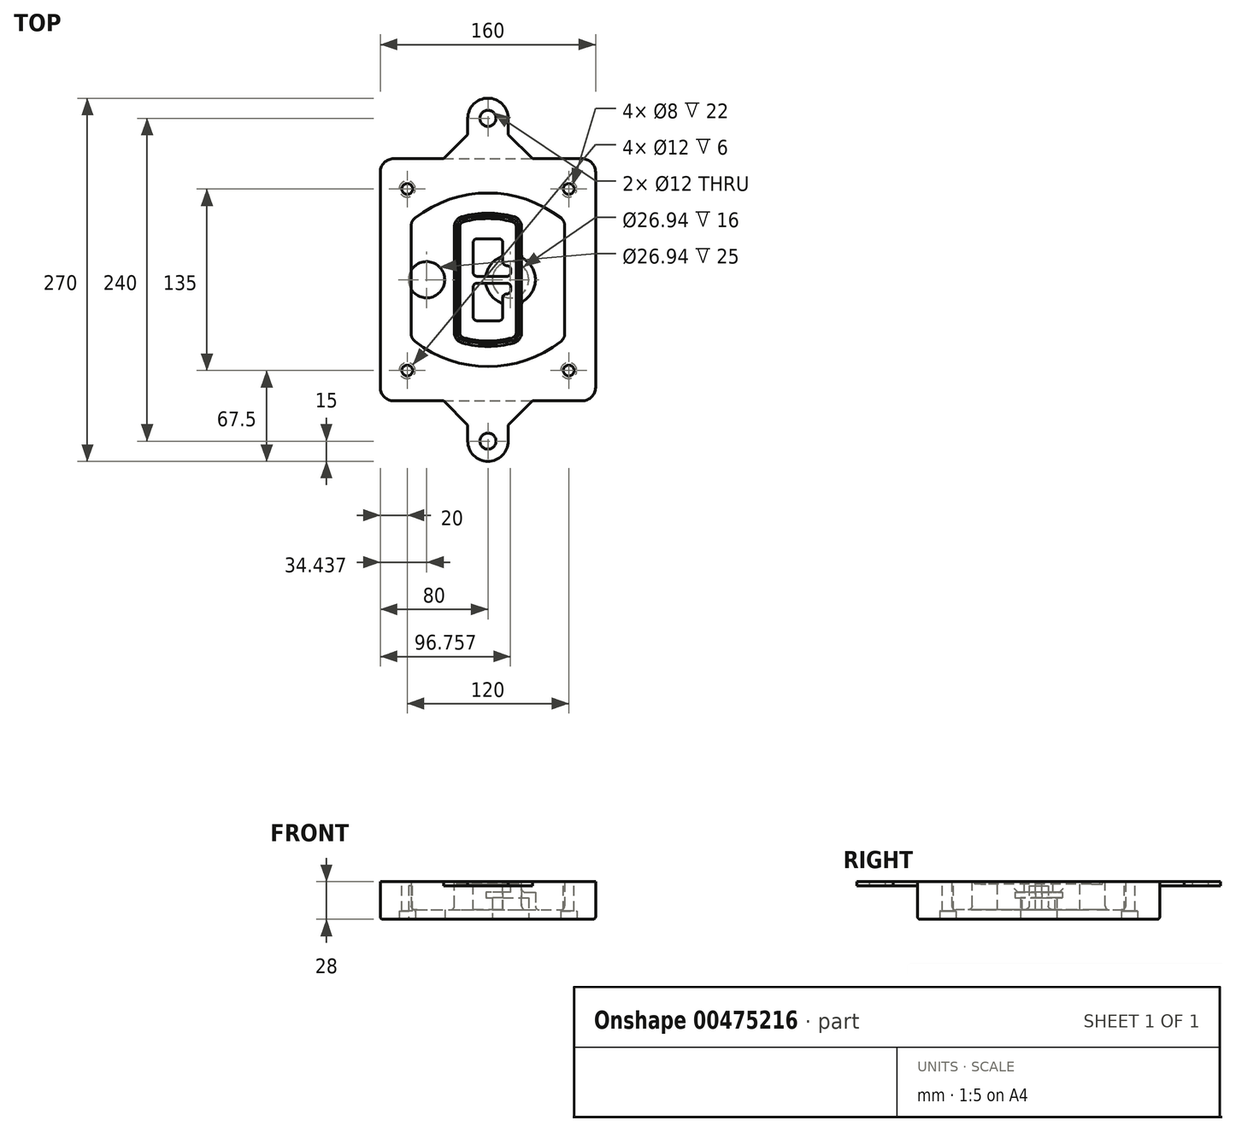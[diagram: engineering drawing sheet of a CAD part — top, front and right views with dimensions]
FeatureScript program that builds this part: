
annotation { "Feature Type Name" : "Feature", "Feature Type Description" : "" }
export const myFeature = defineFeature(function(context is Context, id is Id, definition is map)
    precondition{}
    {
        {
            var Q0;
            Q0=qCreatedBy(makeId("Top.planeOp"),FACE);
            var sketch = newSketch(context, id + "F0", { "sketchPlane" : qUnion([Q0])});
            skPoint(sketch, "E0.rect.middle", {"position": v(0, 0) * mm});
            skLineSegment(sketch, "E1.bottom", {"start": v(-70, -90) * mm, "end": v(70, -90) * mm});
            skLineSegment(sketch, "E1.top", {"start": v(-70, 90) * mm, "end": v(70, 90) * mm});
            skLineSegment(sketch, "E1.left", {"start": v(-80, -80) * mm, "end": v(-80, 80) * mm});
            skLineSegment(sketch, "E1.right", {"start": v(80, -80) * mm, "end": v(80, 80) * mm});
            skLineSegment(sketch, "E2", {"start": v(-80, 90) * mm, "end": v(80, -90) * mm, "construction": true});
            skLineSegment(sketch, "E3", {"start": v(80, 90) * mm, "end": v(-80, -90) * mm, "construction": true});
            skCircle(sketch, "E4", {"center": v(-60, 67.5) * mm, "radius": 4 * mm});
            skCircle(sketch, "E5", {"center": v(60, 67.5) * mm, "radius": 4 * mm});
            skCircle(sketch, "E6", {"center": v(60, -67.5) * mm, "radius": 4 * mm});
            skCircle(sketch, "E7", {"center": v(-60, -67.5) * mm, "radius": 4 * mm});
            skLineSegment(sketch, "E8", {"start": v(-60, 67.5) * mm, "end": v(60, 67.5) * mm, "construction": true});
            skLineSegment(sketch, "E9", {"start": v(60, 67.5) * mm, "end": v(60, -67.5) * mm, "construction": true});
            skLineSegment(sketch, "E10", {"start": v(60, -67.5) * mm, "end": v(-60, -67.5) * mm, "construction": true});
            skLineSegment(sketch, "E11", {"start": v(-60, -67.5) * mm, "end": v(-60, 67.5) * mm, "construction": true});
            skLineSegment(sketch, "E12", {"start": v(-60, 40.3) * mm, "end": v(-60, -40.3) * mm});
            skLineSegment(sketch, "E13", {"start": v(60, 40.3) * mm, "end": v(60, -40.3) * mm});
            skArc(sketch, "E14", {"start": v(56.15, 48.18) * mm, "mid": v(0, 67.5) * mm, "end": v(-56.15, 48.18) * mm});
            skArc(sketch, "E15", {"start": v(-56.15, -48.18) * mm, "mid": v(0, -67.5) * mm, "end": v(56.15, -48.18) * mm});
            skLineSegment(sketch, "E16", {"start": v(-60, 0) * mm, "end": v(60, 0) * mm, "construction": true});
            skPoint(sketch, "E17.visualSharp", {"position": v(-60, -45) * mm});
            skArc(sketch, "E17.filletArc", {"start": v(-60, -40.3) * mm, "mid": v(-58.99, -44.68) * mm, "end": v(-56.15, -48.18) * mm});
            skPoint(sketch, "E18.visualSharp", {"position": v(-60, 45) * mm});
            skArc(sketch, "E18.filletArc", {"start": v(-56.15, 48.18) * mm, "mid": v(-58.99, 44.68) * mm, "end": v(-60, 40.3) * mm});
            skPoint(sketch, "E19.visualSharp", {"position": v(60, 45) * mm});
            skArc(sketch, "E19.filletArc", {"start": v(60, 40.3) * mm, "mid": v(58.99, 44.68) * mm, "end": v(56.15, 48.18) * mm});
            skPoint(sketch, "E20.visualSharp", {"position": v(60, -45) * mm});
            skArc(sketch, "E20.filletArc", {"start": v(56.15, -48.18) * mm, "mid": v(58.99, -44.68) * mm, "end": v(60, -40.3) * mm});
            skPoint(sketch, "E21.visualSharp", {"position": v(-80, 90) * mm});
            skArc(sketch, "E21.filletArc", {"start": v(-70, 90) * mm, "mid": v(-77.07, 87.07) * mm, "end": v(-80, 80) * mm});
            skPoint(sketch, "E22.visualSharp", {"position": v(80, 90) * mm});
            skArc(sketch, "E22.filletArc", {"start": v(80, 80) * mm, "mid": v(77.07, 87.07) * mm, "end": v(70, 90) * mm});
            skPoint(sketch, "E23.visualSharp", {"position": v(80, -90) * mm});
            skArc(sketch, "E23.filletArc", {"start": v(70, -90) * mm, "mid": v(77.07, -87.07) * mm, "end": v(80, -80) * mm});
            skPoint(sketch, "E24.visualSharp", {"position": v(-80, -90) * mm});
            skArc(sketch, "E24.filletArc", {"start": v(-80, -80) * mm, "mid": v(-77.07, -87.07) * mm, "end": v(-70, -90) * mm});
            skArc(sketch, "E25.0", {"start": v(57, 40.3) * mm, "mid": v(56.3, 43.36) * mm, "end": v(54.3, 45.81) * mm});
            skLineSegment(sketch, "E25.1", {"start": v(57, 40.3) * mm, "end": v(57, -40.3) * mm});
            skArc(sketch, "E25.2", {"start": v(54.3, -45.81) * mm, "mid": v(56.3, -43.36) * mm, "end": v(57, -40.3) * mm});
            skArc(sketch, "E25.3", {"start": v(-54.3, -45.81) * mm, "mid": v(0, -64.5) * mm, "end": v(54.3, -45.81) * mm});
            skArc(sketch, "E25.4", {"start": v(-57, -40.3) * mm, "mid": v(-56.3, -43.36) * mm, "end": v(-54.3, -45.81) * mm});
            skArc(sketch, "E25.5", {"start": v(54.3, 45.81) * mm, "mid": v(0, 64.5) * mm, "end": v(-54.3, 45.81) * mm});
            skLineSegment(sketch, "E25.6", {"start": v(-57, 40.3) * mm, "end": v(-57, -40.3) * mm});
            skArc(sketch, "E25.7", {"start": v(-54.3, 45.81) * mm, "mid": v(-56.3, 43.36) * mm, "end": v(-57, 40.3) * mm});
            skArc(sketch, "E26.0", {"start": v(-58.62, 51.33) * mm, "mid": v(-62.58, 46.43) * mm, "end": v(-64, 40.3) * mm});
            skArc(sketch, "E26.1", {"start": v(58.62, 51.33) * mm, "mid": v(0, 71.5) * mm, "end": v(-58.62, 51.33) * mm});
            skArc(sketch, "E26.2", {"start": v(64, 40.3) * mm, "mid": v(62.58, 46.43) * mm, "end": v(58.62, 51.33) * mm});
            skLineSegment(sketch, "E26.3", {"start": v(64, 40.3) * mm, "end": v(64, -40.3) * mm});
            skArc(sketch, "E26.4", {"start": v(58.62, -51.33) * mm, "mid": v(62.58, -46.43) * mm, "end": v(64, -40.3) * mm});
            skLineSegment(sketch, "E26.5", {"start": v(-64, 40.3) * mm, "end": v(-64, -40.3) * mm});
            skArc(sketch, "E26.6", {"start": v(-58.62, -51.33) * mm, "mid": v(0, -71.5) * mm, "end": v(58.62, -51.33) * mm});
            skArc(sketch, "E26.7", {"start": v(-64, -40.3) * mm, "mid": v(-62.58, -46.43) * mm, "end": v(-58.62, -51.33) * mm});
            skSolve(sketch);
        }
        {
            var Q0;
            Q0=makeQuery(id+"F0.imprint","IMPRINT",FACE,{"disambiguationData":[TD([[makeQuery(id+"F0.imprint","IMPRINT",EDGE,{"derivedFrom":sQuery(id+"F0.wireOp",EDGE,"E1.bottom")}),1.0]])]});
            var Q1;
            Q1=makeQuery(id+"F0.imprint","IMPRINT",FACE,{"disambiguationData":[TD([[makeQuery(id+"F0.imprint","IMPRINT",EDGE,{"derivedFrom":sQuery(id+"F0.wireOp",EDGE,"E12")}),1.0]])]});
            var Q2;
            Q2=makeQuery(id+"F0.imprint","IMPRINT",FACE,{"disambiguationData":[TD([[makeQuery(id+"F0.imprint","IMPRINT",EDGE,{"derivedFrom":sQuery(id+"F0.wireOp",EDGE,"E25.0")}),1.0]])]});
            var Q3;
            Q3=makeQuery(id+"F0.imprint","IMPRINT",FACE,{"disambiguationData":[TD([[makeQuery(id+"F0.imprint","IMPRINT",EDGE,{"derivedFrom":sQuery(id+"F0.wireOp",EDGE,"E12")}),-1.0]])]});
            extrude(context, id + "F1", {"entities" : qUnion([Q0, Q1, Q2, Q3]), "oppositeDirection" : true, "depth" : 25 * mm});
        }
        {
            var Q0;
            Q0=makeQuery(id+"F0.imprint","IMPRINT",FACE,{"disambiguationData":[TD([[makeQuery(id+"F0.imprint","IMPRINT",EDGE,{"derivedFrom":sQuery(id+"F0.wireOp",EDGE,"E12")}),1.0]])]});
            extrude(context, id + "F2", {"entities" : qUnion([Q0]), "operationType" : NewBodyOperationType.ADD, "depth" : 3 * mm});
        }
        {
            var Q0;
            Q0=makeQuery(id+"F0.imprint","IMPRINT",FACE,{"disambiguationData":[TD([[makeQuery(id+"F0.imprint","IMPRINT",EDGE,{"derivedFrom":sQuery(id+"F0.wireOp",EDGE,"E25.0")}),1.0]])]});
            extrude(context, id + "F3", {"entities" : qUnion([Q0]), "operationType" : NewBodyOperationType.REMOVE, "oppositeDirection" : true, "depth" : 18 * mm});
        }
        {
            var Q0;
            Q0=makeQuery(id+"F2.opExtrude","CAP_FACE",FACE,{"disambiguationData":[OSD([sQuery(id+"F0.wireOp",EDGE,"E12"),sQuery(id+"F0.wireOp",EDGE,"E13"),sQuery(id+"F0.wireOp",EDGE,"E14"),sQuery(id+"F0.wireOp",EDGE,"E15"),sQuery(id+"F0.wireOp",EDGE,"E17.filletArc"),sQuery(id+"F0.wireOp",EDGE,"E18.filletArc"),sQuery(id+"F0.wireOp",EDGE,"E19.filletArc"),sQuery(id+"F0.wireOp",EDGE,"E20.filletArc"),sQuery(id+"F0.wireOp",EDGE,"E25.0"),sQuery(id+"F0.wireOp",EDGE,"E25.1"),sQuery(id+"F0.wireOp",EDGE,"E25.2"),sQuery(id+"F0.wireOp",EDGE,"E25.3"),sQuery(id+"F0.wireOp",EDGE,"E25.4"),sQuery(id+"F0.wireOp",EDGE,"E25.5"),sQuery(id+"F0.wireOp",EDGE,"E25.6"),sQuery(id+"F0.wireOp",EDGE,"E25.7")])],"isStart":false});
            var sketch = newSketch(context, id + "F4", { "sketchPlane" : qUnion([Q0])});
            skArc(sketch, "E27.0", {"start": v(-19.08, -46.97) * mm, "mid": v(0, -49.5) * mm, "end": v(19.08, -46.97) * mm});
            skArc(sketch, "E28.0", {"start": v(19.08, 46.97) * mm, "mid": v(0, 49.5) * mm, "end": v(-19.08, 46.97) * mm});
            skLineSegment(sketch, "E29", {"start": v(-25, 39.25) * mm, "end": v(-25, -39.25) * mm});
            skLineSegment(sketch, "E30", {"start": v(25, 39.25) * mm, "end": v(25, -39.25) * mm});
            skLineSegment(sketch, "E31", {"start": v(-25, 45.1) * mm, "end": v(25, 45.1) * mm, "construction": true});
            skLineSegment(sketch, "E32", {"start": v(-25, -45.1) * mm, "end": v(25, -45.1) * mm, "construction": true});
            skPoint(sketch, "E33.visualSharp", {"position": v(-25, 45.1) * mm});
            skArc(sketch, "E33.filletArc", {"start": v(-19.08, 46.97) * mm, "mid": v(-23.35, 44.11) * mm, "end": v(-25, 39.25) * mm});
            skPoint(sketch, "E34.visualSharp", {"position": v(25, 45.1) * mm});
            skArc(sketch, "E34.filletArc", {"start": v(25, 39.25) * mm, "mid": v(23.35, 44.11) * mm, "end": v(19.08, 46.97) * mm});
            skPoint(sketch, "E35.visualSharp", {"position": v(25, -45.1) * mm});
            skArc(sketch, "E35.filletArc", {"start": v(19.08, -46.97) * mm, "mid": v(23.35, -44.11) * mm, "end": v(25, -39.25) * mm});
            skPoint(sketch, "E36.visualSharp", {"position": v(-25, -45.1) * mm});
            skArc(sketch, "E36.filletArc", {"start": v(-25, -39.25) * mm, "mid": v(-23.35, -44.11) * mm, "end": v(-19.08, -46.97) * mm});
            skArc(sketch, "E37.0", {"start": v(54.3, 45.81) * mm, "mid": v(0, 64.5) * mm, "end": v(-54.3, 45.81) * mm});
            skArc(sketch, "E37.1", {"start": v(-54.3, 45.81) * mm, "mid": v(-56.3, 43.36) * mm, "end": v(-57, 40.3) * mm});
            skLineSegment(sketch, "E37.2", {"start": v(-57, 40.3) * mm, "end": v(-57, -40.3) * mm});
            skArc(sketch, "E37.3", {"start": v(-57, -40.3) * mm, "mid": v(-56.3, -43.36) * mm, "end": v(-54.3, -45.81) * mm});
            skArc(sketch, "E37.4", {"start": v(-54.3, -45.81) * mm, "mid": v(0, -64.5) * mm, "end": v(54.3, -45.81) * mm});
            skArc(sketch, "E37.5", {"start": v(54.3, -45.81) * mm, "mid": v(56.3, -43.36) * mm, "end": v(57, -40.3) * mm});
            skLineSegment(sketch, "E37.6", {"start": v(57, 40.3) * mm, "end": v(57, -40.3) * mm});
            skArc(sketch, "E37.7", {"start": v(57, 40.3) * mm, "mid": v(56.3, 43.36) * mm, "end": v(54.3, 45.81) * mm});
            skLineSegment(sketch, "E38.0", {"start": v(23, 39.25) * mm, "end": v(23, -39.25) * mm});
            skArc(sketch, "E38.1", {"start": v(18.56, -45.04) * mm, "mid": v(21.76, -42.9) * mm, "end": v(23, -39.25) * mm});
            skArc(sketch, "E38.2", {"start": v(-18.56, -45.04) * mm, "mid": v(0, -47.5) * mm, "end": v(18.56, -45.04) * mm});
            skArc(sketch, "E38.3", {"start": v(-23, -39.25) * mm, "mid": v(-21.76, -42.9) * mm, "end": v(-18.56, -45.04) * mm});
            skLineSegment(sketch, "E38.4", {"start": v(-23, 39.25) * mm, "end": v(-23, -39.25) * mm});
            skArc(sketch, "E38.5", {"start": v(23, 39.25) * mm, "mid": v(21.76, 42.9) * mm, "end": v(18.56, 45.04) * mm});
            skArc(sketch, "E38.6", {"start": v(-18.56, 45.04) * mm, "mid": v(-21.76, 42.9) * mm, "end": v(-23, 39.25) * mm});
            skArc(sketch, "E38.7", {"start": v(18.56, 45.04) * mm, "mid": v(0, 47.5) * mm, "end": v(-18.56, 45.04) * mm});
            skArc(sketch, "E39.0", {"start": v(21, 39.25) * mm, "mid": v(20.18, 41.68) * mm, "end": v(18.04, 43.1) * mm});
            skLineSegment(sketch, "E39.1", {"start": v(21, 39.25) * mm, "end": v(21, -39.25) * mm});
            skArc(sketch, "E39.2", {"start": v(18.04, -43.1) * mm, "mid": v(20.18, -41.68) * mm, "end": v(21, -39.25) * mm});
            skArc(sketch, "E39.3", {"start": v(-18.04, -43.1) * mm, "mid": v(0, -45.5) * mm, "end": v(18.04, -43.1) * mm});
            skArc(sketch, "E39.4", {"start": v(-21, -39.25) * mm, "mid": v(-20.18, -41.68) * mm, "end": v(-18.04, -43.1) * mm});
            skArc(sketch, "E39.5", {"start": v(18.04, 43.1) * mm, "mid": v(0, 45.5) * mm, "end": v(-18.04, 43.1) * mm});
            skLineSegment(sketch, "E39.6", {"start": v(-21, 39.25) * mm, "end": v(-21, -39.25) * mm});
            skArc(sketch, "E39.7", {"start": v(-18.04, 43.1) * mm, "mid": v(-20.18, 41.68) * mm, "end": v(-21, 39.25) * mm});
            skLineSegment(sketch, "E40", {"start": v(-25, 0) * mm, "end": v(25, 0) * mm, "construction": true});
            skLineSegment(sketch, "E41", {"start": v(-11, 5.5) * mm, "end": v(-11, 27.5) * mm});
            skLineSegment(sketch, "E42", {"start": v(-8, 30.5) * mm, "end": v(8, 30.5) * mm});
            skLineSegment(sketch, "E43", {"start": v(11, 27.5) * mm, "end": v(11, 13.5) * mm});
            skLineSegment(sketch, "E44", {"start": v(14, 10.5) * mm, "end": v(14, 10.5) * mm});
            skLineSegment(sketch, "E45", {"start": v(17, 7.5) * mm, "end": v(17, 5.5) * mm});
            skLineSegment(sketch, "E46", {"start": v(14, 2.5) * mm, "end": v(-8, 2.5) * mm});
            skPoint(sketch, "E47.visualSharp", {"position": v(-11, 30.5) * mm});
            skArc(sketch, "E47.filletArc", {"start": v(-8, 30.5) * mm, "mid": v(-10.12, 29.62) * mm, "end": v(-11, 27.5) * mm});
            skPoint(sketch, "E48.visualSharp", {"position": v(11, 30.5) * mm});
            skArc(sketch, "E48.filletArc", {"start": v(11, 27.5) * mm, "mid": v(10.12, 29.62) * mm, "end": v(8, 30.5) * mm});
            skPoint(sketch, "E49.visualSharp", {"position": v(11, 10.5) * mm});
            skArc(sketch, "E49.filletArc", {"start": v(11, 13.5) * mm, "mid": v(11.88, 11.38) * mm, "end": v(14, 10.5) * mm});
            skPoint(sketch, "E50.visualSharp", {"position": v(17, 10.5) * mm});
            skArc(sketch, "E50.filletArc", {"start": v(17, 7.5) * mm, "mid": v(16.12, 9.62) * mm, "end": v(14, 10.5) * mm});
            skPoint(sketch, "E51.visualSharp", {"position": v(17, 2.5) * mm});
            skArc(sketch, "E51.filletArc", {"start": v(14, 2.5) * mm, "mid": v(16.12, 3.38) * mm, "end": v(17, 5.5) * mm});
            skPoint(sketch, "E52.visualSharp", {"position": v(-11, 2.5) * mm});
            skArc(sketch, "E52.filletArc", {"start": v(-11, 5.5) * mm, "mid": v(-10.12, 3.38) * mm, "end": v(-8, 2.5) * mm});
            skLineSegment(sketch, "E53.0.MirrorCS", {"start": v(14, -2.5) * mm, "end": v(-8, -2.5) * mm});
            skArc(sketch, "E54.0.MirrorCS", {"start": v(-11, -5.5) * mm, "mid": v(-10.12, -3.38) * mm, "end": v(-8, -2.5) * mm});
            skLineSegment(sketch, "E55.0.MirrorCS", {"start": v(-11, -5.5) * mm, "end": v(-11, -27.5) * mm});
            skArc(sketch, "E56.0.MirrorCS", {"start": v(-8, -30.5) * mm, "mid": v(-10.12, -29.62) * mm, "end": v(-11, -27.5) * mm});
            skLineSegment(sketch, "E57.0.MirrorCS", {"start": v(-8, -30.5) * mm, "end": v(8, -30.5) * mm});
            skArc(sketch, "E58.0.MirrorCS", {"start": v(11, -27.5) * mm, "mid": v(10.12, -29.62) * mm, "end": v(8, -30.5) * mm});
            skLineSegment(sketch, "E59.0.MirrorCS", {"start": v(11, -27.5) * mm, "end": v(11, -13.5) * mm});
            skArc(sketch, "E60.0.MirrorCS", {"start": v(11, -13.5) * mm, "mid": v(11.88, -11.38) * mm, "end": v(14, -10.5) * mm});
            skArc(sketch, "E61.0.MirrorCS", {"start": v(17, -7.5) * mm, "mid": v(16.12, -9.62) * mm, "end": v(14, -10.5) * mm});
            skLineSegment(sketch, "E62.0.MirrorCS", {"start": v(17, -7.5) * mm, "end": v(17, -5.5) * mm});
            skArc(sketch, "E63.0.MirrorCS", {"start": v(14, -2.5) * mm, "mid": v(16.12, -3.38) * mm, "end": v(17, -5.5) * mm});
            skSolve(sketch);
        }
        {
            var Q0;
            Q0=makeQuery(id+"F4.imprint","IMPRINT",FACE,{"disambiguationData":[TD([[makeQuery(id+"F4.imprint","IMPRINT",EDGE,{"derivedFrom":sQuery(id+"F4.wireOp",EDGE,"E27.0")}),1.0]])]});
            var Q1;
            Q1=makeQuery(id+"F4.imprint","IMPRINT",FACE,{"disambiguationData":[TD([[makeQuery(id+"F4.imprint","IMPRINT",EDGE,{"derivedFrom":sQuery(id+"F4.wireOp",EDGE,"E38.0")}),-1.0]])]});
            var Q2;
            Q2=makeQuery(id+"F4.imprint","IMPRINT",FACE,{"disambiguationData":[TD([[makeQuery(id+"F4.imprint","IMPRINT",EDGE,{"derivedFrom":sQuery(id+"F4.wireOp",EDGE,"E39.0")}),1.0]])]});
            extrude(context, id + "F5", {"entities" : qUnion([Q0, Q1, Q2]), "operationType" : NewBodyOperationType.ADD, "endBound" : BoundingType.UP_TO_NEXT, "oppositeDirection" : true, "depth" : 25 * mm});
        }
        {
            var Q0;
            Q0=makeQuery(id+"F4.imprint","IMPRINT",FACE,{"disambiguationData":[TD([[makeQuery(id+"F4.imprint","IMPRINT",EDGE,{"derivedFrom":sQuery(id+"F4.wireOp",EDGE,"E38.0")}),-1.0]])]});
            extrude(context, id + "F6", {"entities" : qUnion([Q0]), "operationType" : NewBodyOperationType.REMOVE, "oppositeDirection" : true, "depth" : 2 * mm});
        }
        {
            var Q0;
            Q0=makeQuery(id+"F1.opExtrude","CAP_FACE",FACE,{"disambiguationData":[OSD([sQuery(id+"F0.wireOp",EDGE,"E1.bottom"),sQuery(id+"F0.wireOp",EDGE,"E1.top"),sQuery(id+"F0.wireOp",EDGE,"E1.left"),sQuery(id+"F0.wireOp",EDGE,"E1.right"),sQuery(id+"F0.wireOp",EDGE,"E4"),sQuery(id+"F0.wireOp",EDGE,"E5"),sQuery(id+"F0.wireOp",EDGE,"E6"),sQuery(id+"F0.wireOp",EDGE,"E7"),sQuery(id+"F0.wireOp",EDGE,"E21.filletArc"),sQuery(id+"F0.wireOp",EDGE,"E22.filletArc"),sQuery(id+"F0.wireOp",EDGE,"E23.filletArc"),sQuery(id+"F0.wireOp",EDGE,"E24.filletArc")])],"isStart":false});
            var sketch = newSketch(context, id + "F7", { "sketchPlane" : qUnion([Q0])});
            skCircle(sketch, "E64", {"center": v(16.76, 0) * mm, "radius": 13.47 * mm});
            skCircle(sketch, "E65", {"center": v(-45.56, 0) * mm, "radius": 13.47 * mm});
            skLineSegment(sketch, "E66", {"start": v(80, 0) * mm, "end": v(-80, 0) * mm});
            skCircle(sketch, "E67", {"center": v(16.76, 0) * mm, "radius": 18.47 * mm});
            skCircle(sketch, "E68", {"center": v(60, -67.5) * mm, "radius": 6 * mm});
            skCircle(sketch, "E69", {"center": v(-60, -67.5) * mm, "radius": 6 * mm});
            skCircle(sketch, "E70", {"center": v(-60, 67.5) * mm, "radius": 6 * mm});
            skCircle(sketch, "E71", {"center": v(60, 67.5) * mm, "radius": 6 * mm});
            skSolve(sketch);
        }
        {
            var Q0;
            {var subQ1=sQuery(id+"F7.wireOp",EDGE,"E66");var subQ4=sQuery(id+"F7.wireOp",EDGE,"E64");var subQ6=makeQuery(id+"F7.imprint","INTERSECT",VERTEX,{"disambiguationData":[OD(0.0)],"derivedFrom":[subQ4,subQ1]});Q0=makeQuery(id+"F7.imprint","IMPRINT",FACE,{"disambiguationData":[TD([[makeQuery(id+"F7.imprint","IMPRINT",EDGE,{"disambiguationData":[TD([[subQ6,-1.0]])],"derivedFrom":subQ4}),-1.0]])]});}
            var Q1;
            {var subQ0=sQuery(id+"F7.wireOp",EDGE,"E66");var subQ1=sQuery(id+"F7.wireOp",EDGE,"E64");var subQ3=makeQuery(id+"F7.imprint","INTERSECT",VERTEX,{"disambiguationData":[OD(0.0)],"derivedFrom":[subQ1,subQ0]});Q1=makeQuery(id+"F7.imprint","IMPRINT",FACE,{"disambiguationData":[TD([[makeQuery(id+"F7.imprint","IMPRINT",EDGE,{"disambiguationData":[TD([[subQ3,-1.0]])],"derivedFrom":subQ1}),1.0]])]});}
            var Q2;
            {var subQ0=sQuery(id+"F7.wireOp",EDGE,"E66");var subQ1=sQuery(id+"F7.wireOp",EDGE,"E64");var subQ3=makeQuery(id+"F7.imprint","INTERSECT",VERTEX,{"disambiguationData":[OD(0.0)],"derivedFrom":[subQ1,subQ0]});Q2=makeQuery(id+"F7.imprint","IMPRINT",FACE,{"disambiguationData":[TD([[makeQuery(id+"F7.imprint","IMPRINT",EDGE,{"disambiguationData":[TD([[subQ3,1.0]])],"derivedFrom":subQ1}),1.0]])]});}
            var Q3;
            {var subQ1=sQuery(id+"F7.wireOp",EDGE,"E66");var subQ4=sQuery(id+"F7.wireOp",EDGE,"E64");var subQ6=makeQuery(id+"F7.imprint","INTERSECT",VERTEX,{"disambiguationData":[OD(0.0)],"derivedFrom":[subQ4,subQ1]});Q3=makeQuery(id+"F7.imprint","IMPRINT",FACE,{"disambiguationData":[TD([[makeQuery(id+"F7.imprint","IMPRINT",EDGE,{"disambiguationData":[TD([[subQ6,1.0]])],"derivedFrom":subQ4}),-1.0]])]});}
            extrude(context, id + "F8", {"entities" : qUnion([Q0, Q1, Q2, Q3]), "operationType" : NewBodyOperationType.ADD, "oppositeDirection" : true, "depth" : 20 * mm});
        }
        {
            var Q0;
            {var subQ0=sQuery(id+"F7.wireOp",EDGE,"E66");var subQ1=sQuery(id+"F7.wireOp",EDGE,"E64");var subQ3=makeQuery(id+"F7.imprint","INTERSECT",VERTEX,{"disambiguationData":[OD(0.0)],"derivedFrom":[subQ1,subQ0]});Q0=makeQuery(id+"F7.imprint","IMPRINT",FACE,{"disambiguationData":[TD([[makeQuery(id+"F7.imprint","IMPRINT",EDGE,{"disambiguationData":[TD([[subQ3,-1.0]])],"derivedFrom":subQ1}),1.0]])]});}
            var Q1;
            {var subQ0=sQuery(id+"F7.wireOp",EDGE,"E66");var subQ1=sQuery(id+"F7.wireOp",EDGE,"E64");var subQ3=makeQuery(id+"F7.imprint","INTERSECT",VERTEX,{"disambiguationData":[OD(0.0)],"derivedFrom":[subQ1,subQ0]});Q1=makeQuery(id+"F7.imprint","IMPRINT",FACE,{"disambiguationData":[TD([[makeQuery(id+"F7.imprint","IMPRINT",EDGE,{"disambiguationData":[TD([[subQ3,1.0]])],"derivedFrom":subQ1}),1.0]])]});}
            extrude(context, id + "F9", {"entities" : qUnion([Q0, Q1]), "operationType" : NewBodyOperationType.REMOVE, "oppositeDirection" : true, "depth" : 16 * mm});
        }
        {
            var Q0;
            {var subQ0=sQuery(id+"F7.wireOp",EDGE,"E66");var subQ1=sQuery(id+"F7.wireOp",EDGE,"E65");var subQ3=makeQuery(id+"F7.imprint","INTERSECT",VERTEX,{"disambiguationData":[OD(0.0)],"derivedFrom":[subQ1,subQ0]});Q0=makeQuery(id+"F7.imprint","IMPRINT",FACE,{"disambiguationData":[TD([[makeQuery(id+"F7.imprint","IMPRINT",EDGE,{"disambiguationData":[TD([[subQ3,-1.0]])],"derivedFrom":subQ1}),1.0]])]});}
            var Q1;
            {var subQ0=sQuery(id+"F7.wireOp",EDGE,"E66");var subQ1=sQuery(id+"F7.wireOp",EDGE,"E65");var subQ3=makeQuery(id+"F7.imprint","INTERSECT",VERTEX,{"disambiguationData":[OD(0.0)],"derivedFrom":[subQ1,subQ0]});Q1=makeQuery(id+"F7.imprint","IMPRINT",FACE,{"disambiguationData":[TD([[makeQuery(id+"F7.imprint","IMPRINT",EDGE,{"disambiguationData":[TD([[subQ3,1.0]])],"derivedFrom":subQ1}),1.0]])]});}
            extrude(context, id + "F10", {"entities" : qUnion([Q0, Q1]), "operationType" : NewBodyOperationType.REMOVE, "oppositeDirection" : true, "depth" : 25 * mm});
        }
        {
            var Q0;
            Q0=makeQuery(id+"F7.imprint","IMPRINT",FACE,{"disambiguationData":[TD([[makeQuery(id+"F7.imprint","IMPRINT",EDGE,{"derivedFrom":sQuery(id+"F7.wireOp",EDGE,"E68")}),1.0]])]});
            var Q1;
            Q1=makeQuery(id+"F7.imprint","IMPRINT",FACE,{"disambiguationData":[TD([[makeQuery(id+"F7.imprint","IMPRINT",EDGE,{"derivedFrom":makeQuery(id+"F1.opExtrude","CAP_EDGE",EDGE,{"disambiguationData":[OSD([sQuery(id+"F0.wireOp",EDGE,"E5")])],"isStart":false})}),-1.0]])]});
            var Q2;
            Q2=makeQuery(id+"F7.imprint","IMPRINT",FACE,{"disambiguationData":[TD([[makeQuery(id+"F7.imprint","IMPRINT",EDGE,{"derivedFrom":sQuery(id+"F7.wireOp",EDGE,"E69")}),1.0]])]});
            var Q3;
            Q3=makeQuery(id+"F7.imprint","IMPRINT",FACE,{"disambiguationData":[TD([[makeQuery(id+"F7.imprint","IMPRINT",EDGE,{"derivedFrom":makeQuery(id+"F1.opExtrude","CAP_EDGE",EDGE,{"disambiguationData":[OSD([sQuery(id+"F0.wireOp",EDGE,"E4")])],"isStart":false})}),-1.0]])]});
            var Q4;
            Q4=makeQuery(id+"F7.imprint","IMPRINT",FACE,{"disambiguationData":[TD([[makeQuery(id+"F7.imprint","IMPRINT",EDGE,{"derivedFrom":sQuery(id+"F7.wireOp",EDGE,"E70")}),1.0]])]});
            var Q5;
            Q5=makeQuery(id+"F7.imprint","IMPRINT",FACE,{"disambiguationData":[TD([[makeQuery(id+"F7.imprint","IMPRINT",EDGE,{"derivedFrom":makeQuery(id+"F1.opExtrude","CAP_EDGE",EDGE,{"disambiguationData":[OSD([sQuery(id+"F0.wireOp",EDGE,"E7")])],"isStart":false})}),-1.0]])]});
            var Q6;
            Q6=makeQuery(id+"F7.imprint","IMPRINT",FACE,{"disambiguationData":[TD([[makeQuery(id+"F7.imprint","IMPRINT",EDGE,{"derivedFrom":sQuery(id+"F7.wireOp",EDGE,"E71")}),1.0]])]});
            var Q7;
            Q7=makeQuery(id+"F7.imprint","IMPRINT",FACE,{"disambiguationData":[TD([[makeQuery(id+"F7.imprint","IMPRINT",EDGE,{"derivedFrom":makeQuery(id+"F1.opExtrude","CAP_EDGE",EDGE,{"disambiguationData":[OSD([sQuery(id+"F0.wireOp",EDGE,"E6")])],"isStart":false})}),-1.0]])]});
            extrude(context, id + "F11", {"entities" : qUnion([Q0, Q1, Q2, Q3, Q4, Q5, Q6, Q7]), "operationType" : NewBodyOperationType.REMOVE, "oppositeDirection" : true, "depth" : 6 * mm});
        }
        {
            var Q0;
            Q0=makeQuery(id+"F9.boolean.opBoolean","COPY",FACE,{"derivedFrom":makeQuery(id+"F9.opExtrude","CAP_FACE",FACE,{"disambiguationData":[OSD([sQuery(id+"F7.wireOp",EDGE,"E64")])],"isStart":false})});
            var sketch = newSketch(context, id + "F12", { "sketchPlane" : qUnion([Q0])});
            skArc(sketch, "E72.0", {"start": v(11, 17.55) * mm, "mid": v(2.57, 11.82) * mm, "end": v(-1.54, 2.5) * mm});
            skArc(sketch, "E72.1", {"start": v(-1.54, -2.5) * mm, "mid": v(2.57, -11.82) * mm, "end": v(11, -17.55) * mm});
            skLineSegment(sketch, "E73", {"start": v(-1.54, -2.5) * mm, "end": v(14, -2.5) * mm});
            skLineSegment(sketch, "E74.0", {"start": v(14, 2.5) * mm, "end": v(-1.54, 2.5) * mm});
            skArc(sketch, "E74.1", {"start": v(14, 2.5) * mm, "mid": v(16.12, 3.38) * mm, "end": v(17, 5.5) * mm});
            skLineSegment(sketch, "E74.2", {"start": v(17, 7.5) * mm, "end": v(17, 5.5) * mm});
            skArc(sketch, "E74.3", {"start": v(17, 7.5) * mm, "mid": v(16.12, 9.62) * mm, "end": v(14, 10.5) * mm});
            skArc(sketch, "E74.4", {"start": v(11, 13.5) * mm, "mid": v(11.88, 11.38) * mm, "end": v(14, 10.5) * mm});
            skLineSegment(sketch, "E74.5", {"start": v(11, 17.55) * mm, "end": v(11, 13.5) * mm});
            skLineSegment(sketch, "E74.7", {"start": v(14, -2.5) * mm, "end": v(-1.54, -2.5) * mm});
            skArc(sketch, "E74.8", {"start": v(14, -2.5) * mm, "mid": v(16.12, -3.38) * mm, "end": v(17, -5.5) * mm});
            skLineSegment(sketch, "E74.9", {"start": v(17, -7.5) * mm, "end": v(17, -5.5) * mm});
            skArc(sketch, "E74.10", {"start": v(17, -7.5) * mm, "mid": v(16.12, -9.62) * mm, "end": v(14, -10.5) * mm});
            skArc(sketch, "E74.11", {"start": v(11, -13.5) * mm, "mid": v(11.88, -11.38) * mm, "end": v(14, -10.5) * mm});
            skLineSegment(sketch, "E74.12", {"start": v(11, -17.55) * mm, "end": v(11, -13.5) * mm});
            skPoint(sketch, "E75.orphan", {"position": v(11, -27.5) * mm});
            skPoint(sketch, "E76.orphan", {"position": v(-8, -2.5) * mm});
            skPoint(sketch, "E77.orphan", {"position": v(-8, 2.5) * mm});
            skPoint(sketch, "E78.orphan", {"position": v(11, 27.5) * mm});
            skSolve(sketch);
        }
        {
            var Q0;
            {var subQ7=sQuery(id+"F12.wireOp",EDGE,"E72.0");var subQ14=sQuery(id+"F12.wireOp",EDGE,"E72.1");var subQ16=sQuery(id+"F12.wireOp",EDGE,"E74.1");var subQ18=sQuery(id+"F12.wireOp",EDGE,"E74.8");Q0=qUnion([makeQuery(id+"F12.imprint","IMPRINT",FACE,{"disambiguationData":[TD([[makeQuery(id+"F12.imprint","IMPRINT",EDGE,{"derivedFrom":subQ7}),1.0]])]}),makeQuery(id+"F12.imprint","IMPRINT",FACE,{"disambiguationData":[TD([[makeQuery(id+"F12.imprint","IMPRINT",EDGE,{"derivedFrom":subQ14}),1.0]])]}),makeQuery(id+"F12.imprint","IMPRINT",FACE,{"disambiguationData":[TD([[makeQuery(id+"F12.imprint","IMPRINT",EDGE,{"derivedFrom":subQ16}),1.0]])]}),makeQuery(id+"F12.imprint","IMPRINT",FACE,{"disambiguationData":[TD([[makeQuery(id+"F12.imprint","IMPRINT",EDGE,{"derivedFrom":subQ18}),-1.0]])]})]);}
            var Q1;
            Q1=makeQuery(id+"F5.boolean.opBoolean","SPLIT",FACE,{"disambiguationData":[TD([makeQuery(id+"F5.opExtrude","SWEPT_FACE",FACE,{"disambiguationData":[OSD([sQuery(id+"F4.wireOp",EDGE,"E41")])]})])],"derivedFrom":makeQuery(id+"F3.boolean.opBoolean","COPY",FACE,{"derivedFrom":makeQuery(id+"F3.opExtrude","CAP_FACE",FACE,{"disambiguationData":[OSD([sQuery(id+"F0.wireOp",EDGE,"E25.0"),sQuery(id+"F0.wireOp",EDGE,"E25.1"),sQuery(id+"F0.wireOp",EDGE,"E25.2"),sQuery(id+"F0.wireOp",EDGE,"E25.3"),sQuery(id+"F0.wireOp",EDGE,"E25.4"),sQuery(id+"F0.wireOp",EDGE,"E25.5"),sQuery(id+"F0.wireOp",EDGE,"E25.6"),sQuery(id+"F0.wireOp",EDGE,"E25.7")])],"isStart":false})})});
            extrude(context, id + "F13", {"entities" : qUnion([Q0]), "operationType" : NewBodyOperationType.REMOVE, "endBound" : BoundingType.UP_TO_SURFACE, "endBoundEntityFace" : qUnion([Q1]), "depth" : 25 * mm});
        }
        {
            var Q0;
            Q0=makeQuery(id+"F3.boolean.opBoolean","COPY",EDGE,{"derivedFrom":makeQuery(id+"F3.opExtrude","CAP_EDGE",EDGE,{"disambiguationData":[OSD([sQuery(id+"F0.wireOp",EDGE,"E25.6")])],"isStart":false})});
            var Q1;
            Q1=makeQuery(id+"F8.boolean.opBoolean","INTERSECT",EDGE,{"derivedFrom":[makeQuery(id+"F5.opExtrude","SWEPT_FACE",FACE,{"disambiguationData":[OSD([sQuery(id+"F4.wireOp",EDGE,"E30")])]}),makeQuery(id+"F8.opExtrude","CAP_FACE",FACE,{"disambiguationData":[OSD([sQuery(id+"F7.wireOp",EDGE,"E67")])],"isStart":false})]});
            var Q2;
            Q2=makeQuery(id+"F8.boolean.opBoolean","INTERSECT",EDGE,{"disambiguationData":[OD(1.0)],"derivedFrom":[makeQuery(id+"F5.opExtrude","SWEPT_FACE",FACE,{"disambiguationData":[OSD([sQuery(id+"F4.wireOp",EDGE,"E30")])]}),makeQuery(id+"F8.opExtrude","SWEPT_FACE",FACE,{"disambiguationData":[OSD([sQuery(id+"F7.wireOp",EDGE,"E67")])]})]});
            var Q3;
            {var subQ0=sQuery(id+"F4.wireOp",EDGE,"E30");Q3=makeQuery(id+"F8.boolean.opBoolean","SPLIT",EDGE,{"disambiguationData":[TD([makeQuery(id+"F5.opExtrude","SWEPT_FACE",FACE,{"disambiguationData":[OSD([sQuery(id+"F4.wireOp",EDGE,"E35.filletArc")])]})])],"derivedFrom":makeQuery(id+"F5.opExtrude","CAP_EDGE",EDGE,{"disambiguationData":[OSD([subQ0])],"isStart":false})});}
            var Q4;
            {var subQ0=sQuery(id+"F0.wireOp",EDGE,"E25.7");var subQ1=sQuery(id+"F0.wireOp",EDGE,"E25.1");var subQ2=sQuery(id+"F0.wireOp",EDGE,"E25.6");var subQ3=sQuery(id+"F0.wireOp",EDGE,"E25.5");var subQ4=sQuery(id+"F0.wireOp",EDGE,"E25.4");var subQ5=sQuery(id+"F0.wireOp",EDGE,"E25.0");var subQ6=sQuery(id+"F0.wireOp",EDGE,"E25.2");var subQ7=sQuery(id+"F0.wireOp",EDGE,"E25.3");Q4=makeQuery(id+"F8.boolean.opBoolean","INTERSECT",EDGE,{"derivedFrom":[makeQuery(id+"F5.boolean.opBoolean","SPLIT",FACE,{"disambiguationData":[TD([makeQuery(id+"F2.opExtrude","SWEPT_FACE",FACE,{"disambiguationData":[OSD([subQ5])]})])],"derivedFrom":makeQuery(id+"F3.boolean.opBoolean","COPY",FACE,{"derivedFrom":makeQuery(id+"F3.opExtrude","CAP_FACE",FACE,{"disambiguationData":[OSD([subQ5,subQ1,subQ6,subQ7,subQ4,subQ3,subQ2,subQ0])],"isStart":false})})}),makeQuery(id+"F8.opExtrude","SWEPT_FACE",FACE,{"disambiguationData":[OSD([sQuery(id+"F7.wireOp",EDGE,"E67")])]})]});}
            var Q5;
            Q5=makeQuery(id+"F8.boolean.opBoolean","INTERSECT",EDGE,{"disambiguationData":[OD(0.0)],"derivedFrom":[makeQuery(id+"F5.opExtrude","SWEPT_FACE",FACE,{"disambiguationData":[OSD([sQuery(id+"F4.wireOp",EDGE,"E30")])]}),makeQuery(id+"F8.opExtrude","SWEPT_FACE",FACE,{"disambiguationData":[OSD([sQuery(id+"F7.wireOp",EDGE,"E67")])]})]});
            fillet(context, id + "F14", {"entities" : qUnion([Q0, Q1, Q2, Q3, Q4, Q5]), "radius" : 3 * mm, "tangentPropagation" : true, "allowEdgeOverflow" : false});
        }
        {
            var Q0;
            Q0=makeQuery(id+"F1.opExtrude","CAP_EDGE",EDGE,{"disambiguationData":[OSD([sQuery(id+"F0.wireOp",EDGE,"E1.bottom")])],"isStart":false});
            fillet(context, id + "F15", {"entities" : qUnion([Q0]), "radius" : 2 * mm, "tangentPropagation" : true, "allowEdgeOverflow" : false});
        }
        {
            var Q0;
            Q0=qCreatedBy(makeId("Top.planeOp"),FACE);
            var sketch = newSketch(context, id + "F16", { "sketchPlane" : qUnion([Q0])});
            skLineSegment(sketch, "E79.0", {"start": v(-70, 90) * mm, "end": v(70, 90) * mm});
            skArc(sketch, "E79.1", {"start": v(-70, 90) * mm, "mid": v(-77.07, 87.07) * mm, "end": v(-80, 80) * mm});
            skLineSegment(sketch, "E79.2", {"start": v(-80, -80) * mm, "end": v(-80, 80) * mm});
            skArc(sketch, "E79.3", {"start": v(-80, -80) * mm, "mid": v(-77.07, -87.07) * mm, "end": v(-70, -90) * mm});
            skLineSegment(sketch, "E79.4", {"start": v(-70, -90) * mm, "end": v(70, -90) * mm});
            skArc(sketch, "E79.5", {"start": v(70, -90) * mm, "mid": v(77.07, -87.07) * mm, "end": v(80, -80) * mm});
            skLineSegment(sketch, "E79.6", {"start": v(80, -80) * mm, "end": v(80, 80) * mm});
            skArc(sketch, "E79.7", {"start": v(80, 80) * mm, "mid": v(77.07, 87.07) * mm, "end": v(70, 90) * mm});
            skCircle(sketch, "E79.8", {"center": v(-60, 67.5) * mm, "radius": 4 * mm});
            skCircle(sketch, "E79.9", {"center": v(60, 67.5) * mm, "radius": 4 * mm});
            skCircle(sketch, "E79.10", {"center": v(60, -67.5) * mm, "radius": 4 * mm});
            skCircle(sketch, "E79.11", {"center": v(-60, -67.5) * mm, "radius": 4 * mm});
            skArc(sketch, "E79.12", {"start": v(56.15, 48.18) * mm, "mid": v(0, 67.5) * mm, "end": v(-56.15, 48.18) * mm});
            skArc(sketch, "E79.13", {"start": v(-56.15, 48.18) * mm, "mid": v(-58.99, 44.68) * mm, "end": v(-60, 40.3) * mm});
            skLineSegment(sketch, "E79.14", {"start": v(-60, 40.3) * mm, "end": v(-60, -40.3) * mm});
            skArc(sketch, "E79.15", {"start": v(60, 40.3) * mm, "mid": v(58.99, 44.68) * mm, "end": v(56.15, 48.18) * mm});
            skLineSegment(sketch, "E79.16", {"start": v(60, 40.3) * mm, "end": v(60, -40.3) * mm});
            skArc(sketch, "E79.17", {"start": v(56.15, -48.18) * mm, "mid": v(58.99, -44.68) * mm, "end": v(60, -40.3) * mm});
            skArc(sketch, "E79.18", {"start": v(-56.15, -48.18) * mm, "mid": v(0, -67.5) * mm, "end": v(56.15, -48.18) * mm});
            skArc(sketch, "E79.19", {"start": v(-60, -40.3) * mm, "mid": v(-58.99, -44.68) * mm, "end": v(-56.15, -48.18) * mm});
            skLineSegment(sketch, "E80", {"start": v(0, 90) * mm, "end": v(0, 120) * mm, "construction": true});
            skLineSegment(sketch, "E81", {"start": v(15, 120) * mm, "end": v(15, 108) * mm});
            skLineSegment(sketch, "E82", {"start": v(15, 108) * mm, "end": v(33, 90) * mm});
            skLineSegment(sketch, "E83", {"start": v(-15, 120) * mm, "end": v(-15, 108) * mm});
            skLineSegment(sketch, "E84", {"start": v(-15, 108) * mm, "end": v(-33, 90) * mm});
            skCircle(sketch, "E85", {"center": v(0, 120) * mm, "radius": 6 * mm});
            skArc(sketch, "E86", {"start": v(15, 120) * mm, "mid": v(0, 135) * mm, "end": v(-15, 120) * mm});
            skLineSegment(sketch, "E87", {"start": v(-80, 0) * mm, "end": v(80, 0) * mm});
            skLineSegment(sketch, "E88.MirrorCS", {"start": v(15, -108) * mm, "end": v(33, -90) * mm});
            skLineSegment(sketch, "E89.MirrorCS", {"start": v(-15, -108) * mm, "end": v(-33, -90) * mm});
            skLineSegment(sketch, "E90.MirrorCS", {"start": v(-15, -120) * mm, "end": v(-15, -108) * mm});
            skArc(sketch, "E91.MirrorCS", {"start": v(15, -120) * mm, "mid": v(0, -135) * mm, "end": v(-15, -120) * mm});
            skCircle(sketch, "E92.MirrorC", {"center": v(0, -120) * mm, "radius": 6 * mm});
            skLineSegment(sketch, "E93.MirrorCS", {"start": v(0, -90) * mm, "end": v(0, -120) * mm, "construction": true});
            skLineSegment(sketch, "E94.MirrorCS", {"start": v(15, -120) * mm, "end": v(15, -108) * mm});
            skSolve(sketch);
        }
        {
            var Q0;
            Q0=makeQuery(id+"F16.imprint","IMPRINT",FACE,{"disambiguationData":[TD([[makeQuery(id+"F16.imprint","IMPRINT",EDGE,{"derivedFrom":sQuery(id+"F16.wireOp",EDGE,"E81")}),-1.0]])]});
            var Q1;
            {var subQ1=sQuery(id+"F16.wireOp",EDGE,"E79.1");Q1=makeQuery(id+"F16.imprint","IMPRINT",FACE,{"disambiguationData":[TD([[makeQuery(id+"F16.imprint","IMPRINT",EDGE,{"derivedFrom":subQ1}),1.0]])]});}
            var Q2;
            {var subQ11=sQuery(id+"F16.wireOp",EDGE,"E79.3");Q2=makeQuery(id+"F16.imprint","IMPRINT",FACE,{"disambiguationData":[TD([[makeQuery(id+"F16.imprint","IMPRINT",EDGE,{"derivedFrom":subQ11}),1.0]])]});}
            var Q3;
            {var subQ0=sQuery(id+"F16.wireOp",EDGE,"E88.MirrorCS");Q3=makeQuery(id+"F16.imprint","IMPRINT",FACE,{"disambiguationData":[TD([[makeQuery(id+"F16.imprint","IMPRINT",EDGE,{"derivedFrom":subQ0}),1.0]])]});}
            var Q4;
            Q4=makeQuery(id+"F2.opExtrude","CAP_FACE",FACE,{"disambiguationData":[OSD([sQuery(id+"F0.wireOp",EDGE,"E12"),sQuery(id+"F0.wireOp",EDGE,"E13"),sQuery(id+"F0.wireOp",EDGE,"E14"),sQuery(id+"F0.wireOp",EDGE,"E15"),sQuery(id+"F0.wireOp",EDGE,"E17.filletArc"),sQuery(id+"F0.wireOp",EDGE,"E18.filletArc"),sQuery(id+"F0.wireOp",EDGE,"E19.filletArc"),sQuery(id+"F0.wireOp",EDGE,"E20.filletArc"),sQuery(id+"F0.wireOp",EDGE,"E25.0"),sQuery(id+"F0.wireOp",EDGE,"E25.1"),sQuery(id+"F0.wireOp",EDGE,"E25.2"),sQuery(id+"F0.wireOp",EDGE,"E25.3"),sQuery(id+"F0.wireOp",EDGE,"E25.4"),sQuery(id+"F0.wireOp",EDGE,"E25.5"),sQuery(id+"F0.wireOp",EDGE,"E25.6"),sQuery(id+"F0.wireOp",EDGE,"E25.7")])],"isStart":false});
            extrude(context, id + "F17", {"entities" : qUnion([Q0, Q1, Q2, Q3]), "operationType" : NewBodyOperationType.ADD, "endBound" : BoundingType.UP_TO_SURFACE, "endBoundEntityFace" : qUnion([Q4]), "depth" : 25 * mm});
        }
    });
